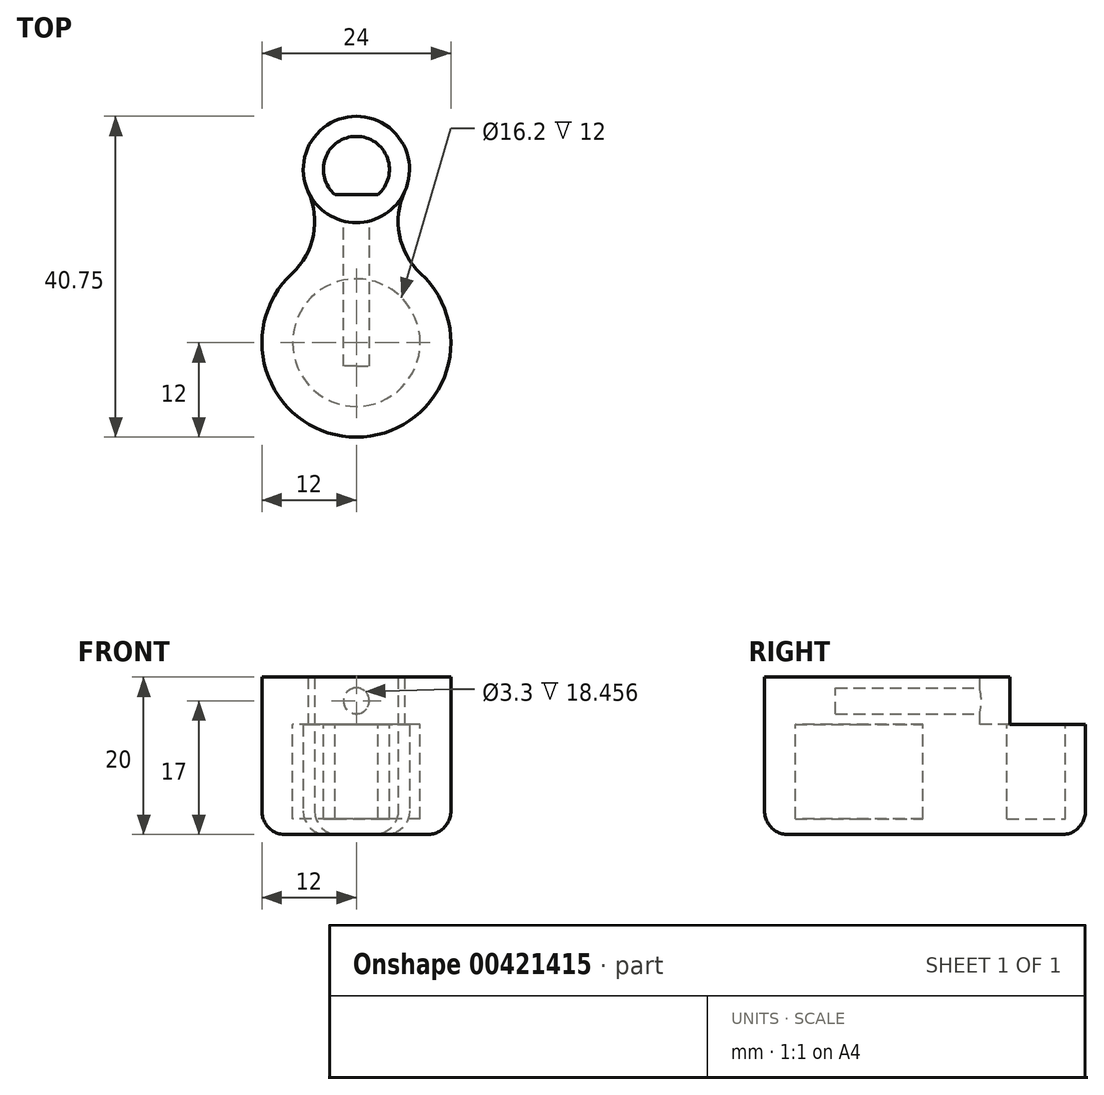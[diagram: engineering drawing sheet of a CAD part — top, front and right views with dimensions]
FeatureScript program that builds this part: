
annotation { "Feature Type Name" : "Feature", "Feature Type Description" : "" }
export const myFeature = defineFeature(function(context is Context, id is Id, definition is map)
    precondition{}
    {
        {
            var Q0;
            Q0=qCreatedBy(makeId("Top.planeOp"),FACE);
            var sketch = newSketch(context, id + "F0", { "sketchPlane" : qUnion([Q0])});
            skArc(sketch, "E0", {"start": v(0, 6.75) * mm, "mid": v(5.69, 3.63) * mm, "end": v(6.13, -2.84) * mm});
            skArc(sketch, "E1", {"start": v(0, -10) * mm, "mid": v(4.39, -10.83) * mm, "end": v(8.17, -13.2) * mm, "construction": true});
            skArc(sketch, "E2", {"start": v(6.13, -2.84) * mm, "mid": v(5.46, -8.35) * mm, "end": v(8.17, -13.2) * mm});
            skLineSegment(sketch, "E3", {"start": v(0, -34) * mm, "end": v(0, -10) * mm});
            skLineSegment(sketch, "E4", {"start": v(0, -10) * mm, "end": v(0, -6.75) * mm});
            skLineSegment(sketch, "E5", {"start": v(0, -6.75) * mm, "end": v(0, 6.75) * mm});
            skArc(sketch, "E6", {"start": v(8.17, -13.2) * mm, "mid": v(11.17, -26.39) * mm, "end": v(0, -34) * mm});
            skArc(sketch, "E7", {"start": v(6.13, -2.84) * mm, "mid": v(3.63, -5.69) * mm, "end": v(0, -6.75) * mm, "construction": true});
            skSolve(sketch);
        }
        {
            var Q0;
            Q0=qSketchRegion(id+"F0",true);
            extrude(context, id + "F1", {"entities" : qUnion([Q0]), "depth" : 14 * mm});
        }
        {
            var Q0;
            Q0=makeQuery(id+"F1.opExtrude","CAP_FACE",FACE,{"disambiguationData":[OSD([sQuery(id+"F0.wireOp",EDGE,"E0"),sQuery(id+"F0.wireOp",EDGE,"E2"),sQuery(id+"F0.wireOp",EDGE,"E3"),sQuery(id+"F0.wireOp",EDGE,"E4"),sQuery(id+"F0.wireOp",EDGE,"E5"),sQuery(id+"F0.wireOp",EDGE,"E6")])],"isStart":false});
            var sketch = newSketch(context, id + "F2", { "sketchPlane" : qUnion([Q0])});
            skArc(sketch, "E8", {"start": v(0, 6.75) * mm, "mid": v(6.75, 0) * mm, "end": v(0, -6.75) * mm});
            skSolve(sketch);
        }
        {
            var Q0;
            {var subQ0=sQuery(id+"F2.wireOp",EDGE,"E8");var subQ3=makeQuery(id+"F2.imprint","INTERSECT",VERTEX,{"derivedFrom":[makeQuery(id+"F1.opExtrude","CAP_EDGE",EDGE,{"disambiguationData":[OSD([sQuery(id+"F0.wireOp",EDGE,"E2")])],"isStart":false}),subQ0]});Q0=makeQuery(id+"F2.imprint","IMPRINT",FACE,{"disambiguationData":[TD([[makeQuery(id+"F2.imprint","IMPRINT",EDGE,{"disambiguationData":[TD([[subQ3,1.0]])],"derivedFrom":subQ0}),-1.0]])]});}
            extrude(context, id + "F3", {"entities" : qUnion([Q0]), "operationType" : NewBodyOperationType.ADD, "depth" : 6 * mm});
        }
        {
            var Q0;
            Q0=makeQuery(id+"F1.opExtrude","SWEPT_BODY",BODY,{"disambiguationData":[OSD([sQuery(id+"F0.wireOp",EDGE,"E0"),sQuery(id+"F0.wireOp",EDGE,"E2"),sQuery(id+"F0.wireOp",EDGE,"E3"),sQuery(id+"F0.wireOp",EDGE,"E4"),sQuery(id+"F0.wireOp",EDGE,"E5"),sQuery(id+"F0.wireOp",EDGE,"E6")])]});
            var Q1;
            Q1=qCreatedBy(makeId("Right.planeOp"),FACE);
            mirror(context, id + "F4", {"operationType" : NewBodyOperationType.ADD, "entities" : qUnion([Q0]), "mirrorPlane" : qUnion([Q1])});
        }
        {
            var Q0;
            {var subQ0=makeQuery(id+"F3.opExtrude","CAP_FACE",FACE,{"disambiguationData":[OSD([sQuery(id+"F0.wireOp",EDGE,"E3"),sQuery(id+"F0.wireOp",EDGE,"E4"),sQuery(id+"F0.wireOp",EDGE,"E5"),sQuery(id+"F2.wireOp",EDGE,"E8")])],"isStart":false});Q0=makeQuery(id+"F4.boolean.opBoolean","MERGE",FACE,{"derivedFrom":[subQ0,makeQuery(id+"F4.opPattern","COPY",FACE,{"derivedFrom":subQ0,"instanceName":"1"})]});}
            var sketch = newSketch(context, id + "F5", { "sketchPlane" : qUnion([Q0])});
            skLineSegment(sketch, "E9", {"start": v(-2.72, -3.2) * mm, "end": v(2.72, -3.2) * mm});
            skArc(sketch, "E10", {"start": v(-2.72, -3.2) * mm, "mid": v(0, -4.2) * mm, "end": v(2.72, -3.2) * mm, "construction": true});
            skArc(sketch, "E11", {"start": v(2.72, -3.2) * mm, "mid": v(0, 4.2) * mm, "end": v(-2.72, -3.2) * mm});
            skSolve(sketch);
        }
        {
            var Q0;
            Q0=qSketchRegion(id+"F5",true);
            extrude(context, id + "F6", {"entities" : qUnion([Q0]), "operationType" : NewBodyOperationType.REMOVE, "oppositeDirection" : true, "depth" : 18 * mm});
        }
        {
            var Q0;
            Q0=qCreatedBy(makeId("Front.planeOp"),FACE);
            var sketch = newSketch(context, id + "F7", { "sketchPlane" : qUnion([Q0])});
            skCircle(sketch, "E12", {"center": v(0, 17) * mm, "radius": 1.65 * mm});
            skSolve(sketch);
        }
        {
            var Q0;
            Q0=qSketchRegion(id+"F7",true);
            extrude(context, id + "F8", {"entities" : qUnion([Q0]), "operationType" : NewBodyOperationType.REMOVE, "depth" : 25 * mm});
        }
        {
            var Q0;
            {var subQ0=makeQuery(id+"F1.opExtrude","CAP_FACE",FACE,{"disambiguationData":[OSD([sQuery(id+"F0.wireOp",EDGE,"E0"),sQuery(id+"F0.wireOp",EDGE,"E2"),sQuery(id+"F0.wireOp",EDGE,"E3"),sQuery(id+"F0.wireOp",EDGE,"E4"),sQuery(id+"F0.wireOp",EDGE,"E5"),sQuery(id+"F0.wireOp",EDGE,"E6")])],"isStart":false});Q0=makeQuery(id+"F4.boolean.opBoolean","MERGE",FACE,{"derivedFrom":[subQ0,makeQuery(id+"F4.opPattern","COPY",FACE,{"derivedFrom":subQ0,"instanceName":"1"})]});}
            var sketch = newSketch(context, id + "F9", { "sketchPlane" : qUnion([Q0])});
            skCircle(sketch, "E13", {"center": v(0, -22) * mm, "radius": 8.1 * mm});
            skSolve(sketch);
        }
        {
            var Q0;
            Q0=qSketchRegion(id+"F9",true);
            extrude(context, id + "F10", {"entities" : qUnion([Q0]), "operationType" : NewBodyOperationType.REMOVE, "oppositeDirection" : true, "depth" : 12 * mm});
        }
        {
            var Q0;
            {var subQ0=makeQuery(id+"F1.opExtrude","CAP_EDGE",EDGE,{"disambiguationData":[OSD([sQuery(id+"F0.wireOp",EDGE,"E0")])],"isStart":true});Q0=makeQuery(id+"F4.boolean.opBoolean","MERGE",EDGE,{"derivedFrom":[subQ0,makeQuery(id+"F4.opPattern","COPY",EDGE,{"derivedFrom":subQ0,"instanceName":"1"})]});}
            var Q1;
            Q1=makeQuery(id+"F1.opExtrude","CAP_EDGE",EDGE,{"disambiguationData":[OSD([sQuery(id+"F0.wireOp",EDGE,"E2")])],"isStart":true});
            var Q2;
            {var subQ0=makeQuery(id+"F1.opExtrude","CAP_EDGE",EDGE,{"disambiguationData":[OSD([sQuery(id+"F0.wireOp",EDGE,"E6")])],"isStart":true});Q2=makeQuery(id+"F4.boolean.opBoolean","MERGE",EDGE,{"derivedFrom":[subQ0,makeQuery(id+"F4.opPattern","COPY",EDGE,{"derivedFrom":subQ0,"instanceName":"1"})]});}
            var Q3;
            Q3=makeQuery(id+"F4.opPattern","COPY",EDGE,{"derivedFrom":makeQuery(id+"F1.opExtrude","CAP_EDGE",EDGE,{"disambiguationData":[OSD([sQuery(id+"F0.wireOp",EDGE,"E2")])],"isStart":true}),"instanceName":"1"});
            var Q4;
            {var subQ0=makeQuery(id+"F1.opExtrude","CAP_EDGE",EDGE,{"disambiguationData":[OSD([sQuery(id+"F0.wireOp",EDGE,"E6")])],"isStart":false});Q4=makeQuery(id+"F4.boolean.opBoolean","MERGE",EDGE,{"derivedFrom":[subQ0,makeQuery(id+"F4.opPattern","COPY",EDGE,{"derivedFrom":subQ0,"instanceName":"1"})]});}
            fillet(context, id + "F11", {"entities" : qUnion([Q0, Q1, Q2, Q3, Q4]), "radius" : 3 * mm, "tangentPropagation" : true, "allowEdgeOverflow" : false});
        }
    });
